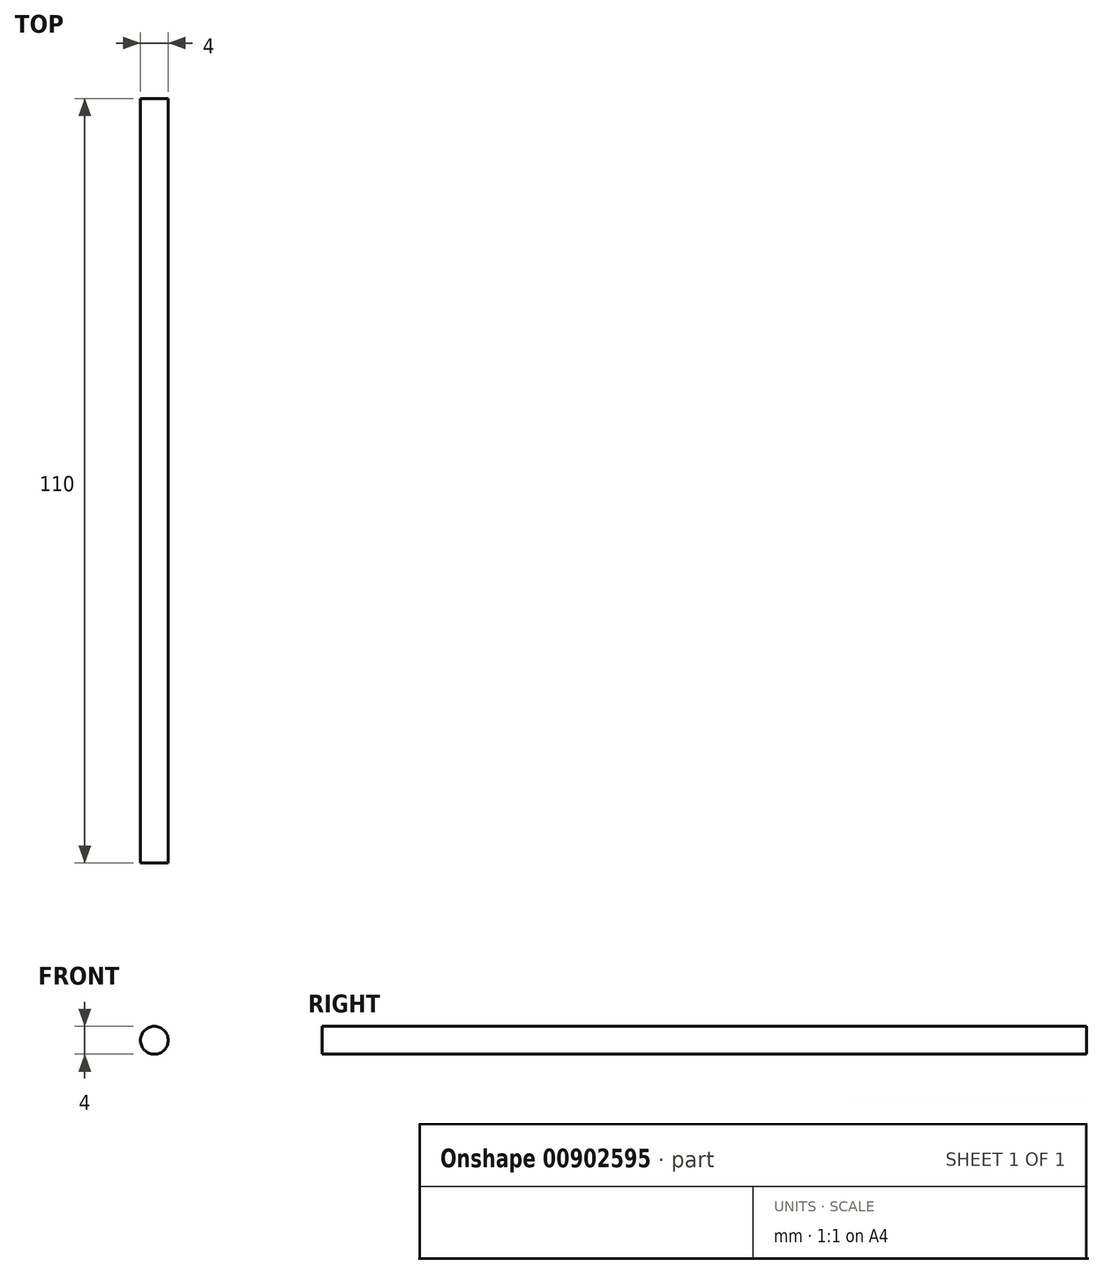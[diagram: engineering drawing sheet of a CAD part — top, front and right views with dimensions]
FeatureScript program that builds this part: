
annotation { "Feature Type Name" : "Feature", "Feature Type Description" : "" }
export const myFeature = defineFeature(function(context is Context, id is Id, definition is map)
    precondition{}
    {
        {
            var Q0;
            Q0=qCreatedBy(makeId("Front.planeOp"),FACE);
            var sketch = newSketch(context, id + "F0", { "sketchPlane" : qUnion([Q0])});
            skCircle(sketch, "E0", {"center": v(0, 0) * mm, "radius": 2 * mm});
            skSolve(sketch);
        }
        {
            var Q0;
            Q0=makeQuery(id+"F0.imprint","IMPRINT",FACE,{"disambiguationData":[TD([[makeQuery(id+"F0.imprint","IMPRINT",EDGE,{"derivedFrom":sQuery(id+"F0.wireOp",EDGE,"E0")}),1.0]])]});
            extrude(context, id + "F1", {"entities" : qUnion([Q0]), "endBound" : BoundingType.SYMMETRIC, "depth" : 110 * mm, "offsetDistance" : 25 * mm});
        }
    });
